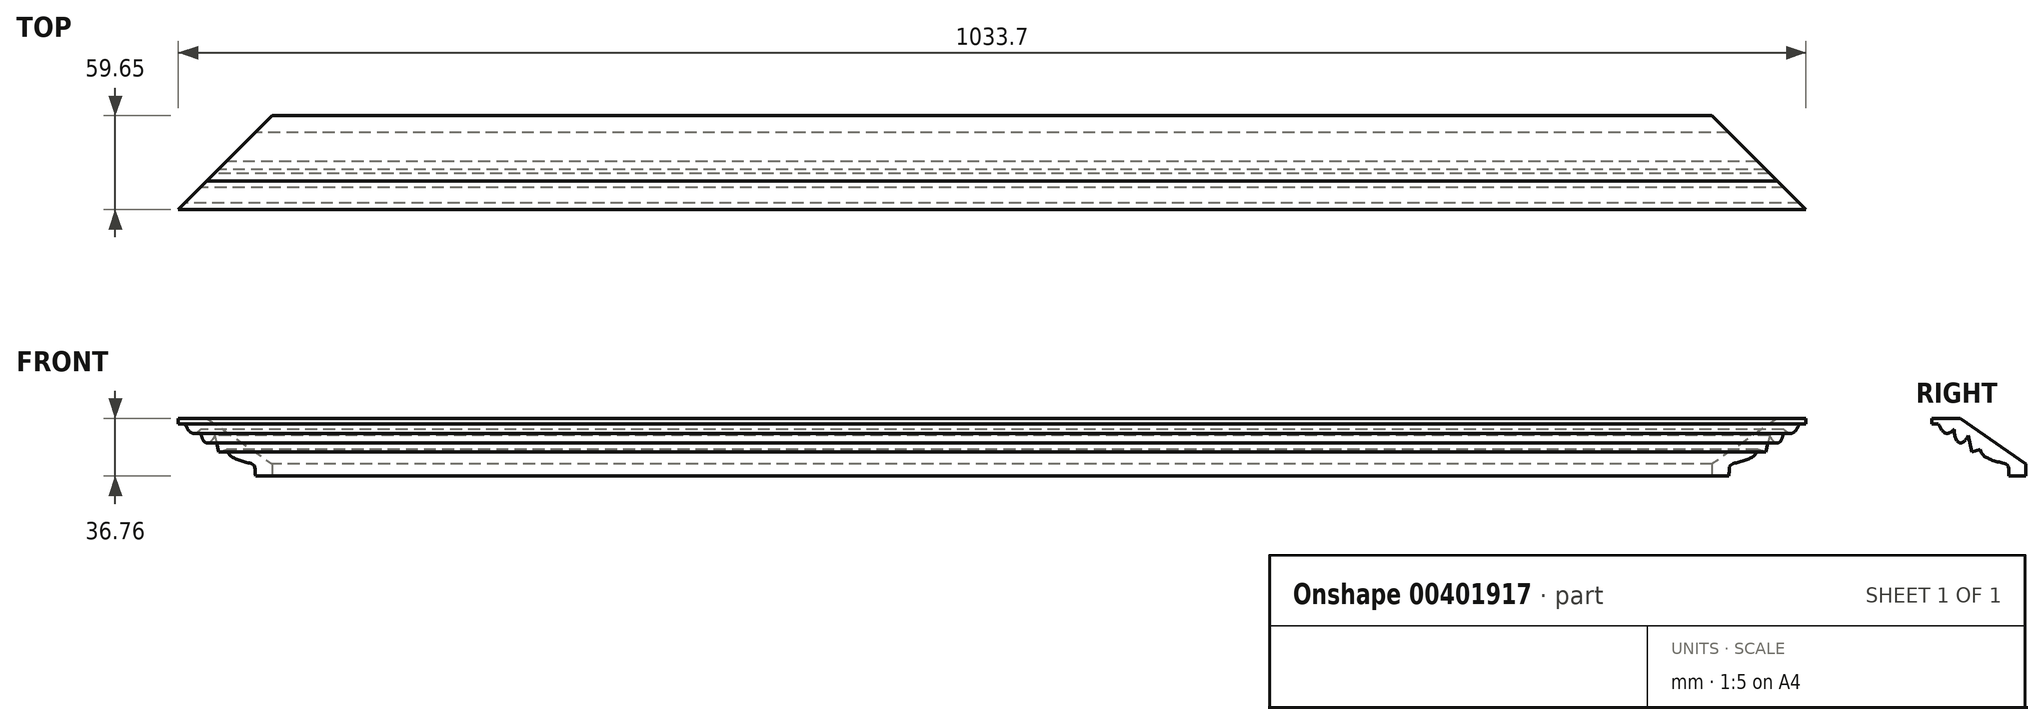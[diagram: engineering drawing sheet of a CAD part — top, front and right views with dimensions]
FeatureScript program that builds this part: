
annotation { "Feature Type Name" : "Feature", "Feature Type Description" : "" }
export const myFeature = defineFeature(function(context is Context, id is Id, definition is map)
    precondition{}
    {
        {
            var Q0;
            Q0=qCreatedBy(makeId("Right.planeOp"),FACE);
            var sketch = newSketch(context, id + "F0", { "sketchPlane" : qUnion([Q0])});
            skLineSegment(sketch, "E0", {"start": v(0, 7.62) * mm, "end": v(-41.61, 36.76) * mm});
            skLineSegment(sketch, "E1", {"start": v(-41.61, 36.76) * mm, "end": v(-59.65, 36.76) * mm});
            skLineSegment(sketch, "E2", {"start": v(-59.65, 36.76) * mm, "end": v(-59.65, 33.27) * mm});
            skLineSegment(sketch, "E3", {"start": v(-59.65, 33.27) * mm, "end": v(-55.58, 33.27) * mm});
            skLineSegment(sketch, "E4", {"start": v(0, 7.62) * mm, "end": v(0, 0) * mm});
            skLineSegment(sketch, "E5", {"start": v(0, 0) * mm, "end": v(-10.67, 0) * mm});
            skFitSpline(sketch, "E6", {"points": [v(-10.67, 0) * mm, v(-11.07, 5.87) * mm, v(-13.33, 7.9) * mm, v(-29.01, 17.09) * mm], "startDerivative": vector(-5.08, 29.03) * mm, "endDerivative": vector(-6.54, 39.72) * mm});
            skLineSegment(sketch, "E7", {"start": v(-29.01, 17.09) * mm, "end": v(-34.16, 15.48) * mm});
            skLineSegment(sketch, "E8", {"start": v(-34.16, 15.48) * mm, "end": v(-36.6, 25.71) * mm});
            skFitSpline(sketch, "E9", {"points": [v(-45.57, 29.68) * mm, v(-52.47, 28.3) * mm, v(-55.58, 33.27) * mm], "startDerivative": vector(-24.15, -24.15) * mm, "endDerivative": vector(-16.65, 31.11) * mm});
            skFitSpline(sketch, "E10", {"points": [v(-45.57, 29.68) * mm, v(-36.6, 25.71) * mm], "startDerivative": vector(2.07, -32.09) * mm, "endDerivative": vector(9.32, 20.18) * mm});
            skSolve(sketch);
        }
        {
            var Q0;
            Q0=qSketchRegion(id+"F0",true);
            extrude(context, id + "F1", {"entities" : qUnion([Q0]), "depth" : 533.4 * mm, "hasSecondDirection" : true, "secondDirectionOppositeDirection" : true, "secondDirectionDepth" : 533.4 * mm});
        }
        {
            var Q0;
            Q0=qCreatedBy(makeId("Top.planeOp"),FACE);
            var sketch = newSketch(context, id + "F2", { "sketchPlane" : qUnion([Q0])});
            skLineSegment(sketch, "E11", {"start": v(-457.2, 0) * mm, "end": v(457.2, 0) * mm, "construction": true});
            skLineSegment(sketch, "E12", {"start": v(457.2, 0) * mm, "end": v(539.77, 0) * mm});
            skLineSegment(sketch, "E13", {"start": v(539.77, 0) * mm, "end": v(539.77, -82.57) * mm});
            skLineSegment(sketch, "E14", {"start": v(539.77, -82.57) * mm, "end": v(457.2, 0) * mm});
            skLineSegment(sketch, "E15", {"start": v(0, 0) * mm, "end": v(0, -141.75) * mm, "construction": true});
            skLineSegment(sketch, "E16.MirrorCS", {"start": v(-457.2, 0) * mm, "end": v(-539.77, 0) * mm});
            skLineSegment(sketch, "E17.MirrorCS", {"start": v(-539.77, -82.57) * mm, "end": v(-457.2, 0) * mm});
            skLineSegment(sketch, "E18.MirrorCS", {"start": v(-539.77, 0) * mm, "end": v(-539.77, -82.57) * mm});
            skSolve(sketch);
        }
        {
            var Q0;
            Q0=qSketchRegion(id+"F2",true);
            extrude(context, id + "F3", {"entities" : qUnion([Q0]), "operationType" : NewBodyOperationType.REMOVE, "endBound" : BoundingType.THROUGH_ALL, "depth" : 25.4 * mm});
        }
    });
